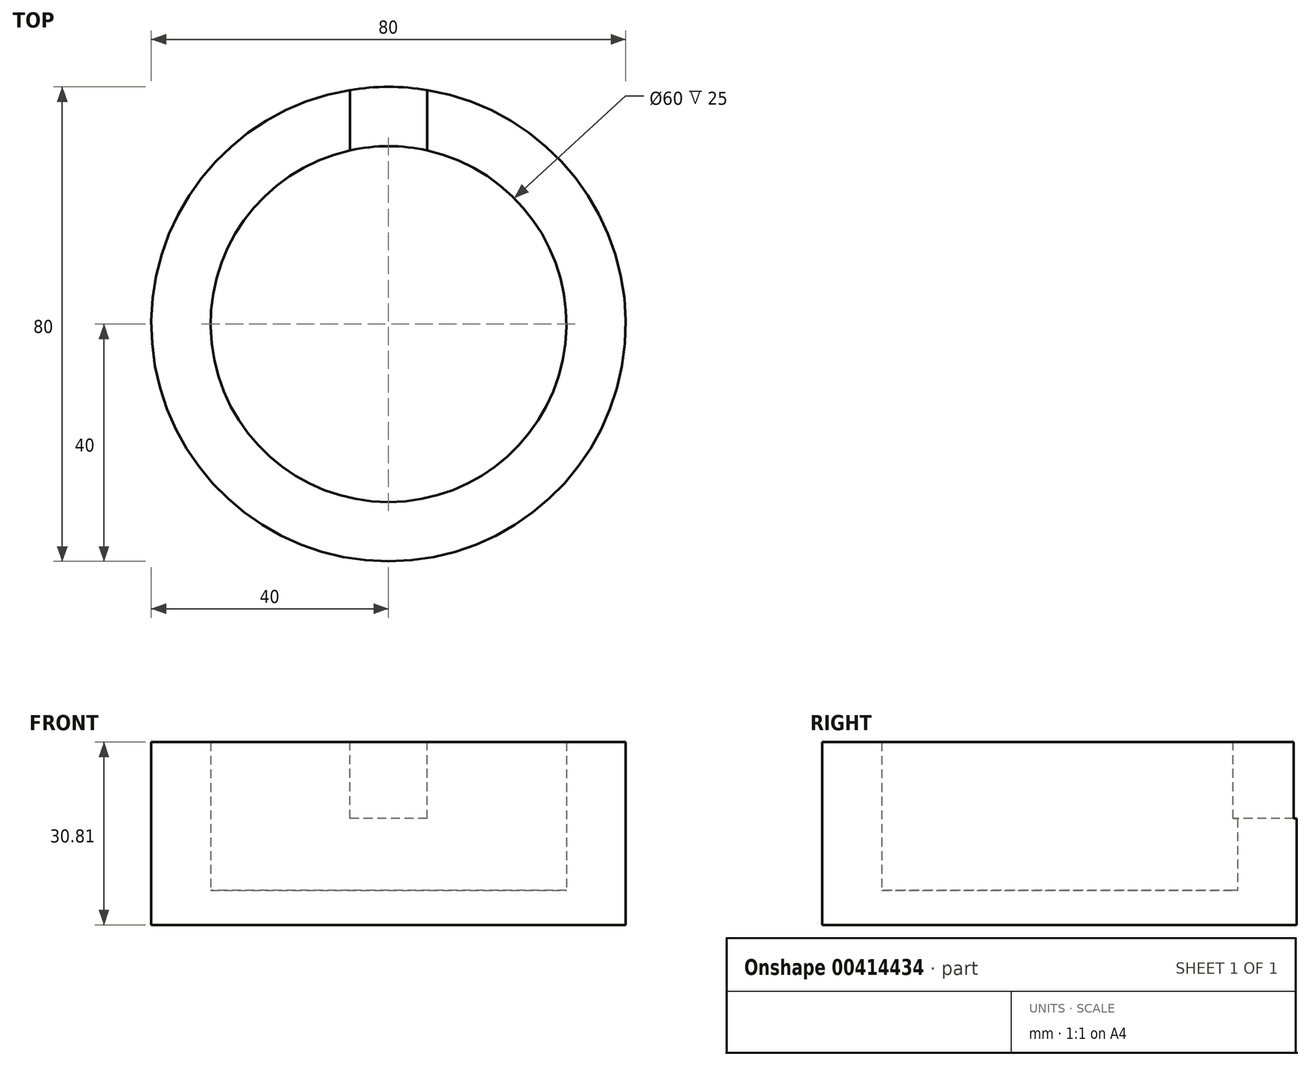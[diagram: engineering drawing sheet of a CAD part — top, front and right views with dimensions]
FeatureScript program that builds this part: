
annotation { "Feature Type Name" : "Feature", "Feature Type Description" : "" }
export const myFeature = defineFeature(function(context is Context, id is Id, definition is map)
    precondition{}
    {
        {
            var Q0;
            Q0=qCreatedBy(makeId("Top.planeOp"),FACE);
            var sketch = newSketch(context, id + "F0", { "sketchPlane" : qUnion([Q0])});
            skCircle(sketch, "E0", {"center": v(0, 0) * mm, "radius": 30 * mm});
            skCircle(sketch, "E1", {"center": v(0, 0) * mm, "radius": 40 * mm});
            skSolve(sketch);
        }
        {
            var Q0;
            Q0=makeQuery(id+"F0.imprint","IMPRINT",FACE,{"disambiguationData":[TD([[makeQuery(id+"F0.imprint","IMPRINT",EDGE,{"derivedFrom":sQuery(id+"F0.wireOp",EDGE,"E0")}),-1.0]])]});
            extrude(context, id + "F1", {"entities" : qUnion([Q0]), "depth" : 25 * mm});
        }
        {
            var Q0;
            Q0=makeQuery(id+"F1.opExtrude","CAP_FACE",FACE,{"disambiguationData":[OSD([sQuery(id+"F0.wireOp",EDGE,"E0"),sQuery(id+"F0.wireOp",EDGE,"E1")])],"isStart":false});
            var sketch = newSketch(context, id + "F2", { "sketchPlane" : qUnion([Q0])});
            skLineSegment(sketch, "E2", {"start": v(6.5, 39.47) * mm, "end": v(6.5, 29.29) * mm});
            skArc(sketch, "E3", {"start": v(6.5, 29.29) * mm, "mid": v(3.27, 29.82) * mm, "end": v(0, 30) * mm});
            skLineSegment(sketch, "E4", {"start": v(0, 30) * mm, "end": v(0, 40) * mm, "construction": true});
            skArc(sketch, "E5", {"start": v(6.5, 39.47) * mm, "mid": v(3.26, 39.87) * mm, "end": v(0, 40) * mm});
            skArc(sketch, "E6.MirrorCS", {"start": v(-6.5, 39.47) * mm, "mid": v(-3.26, 39.87) * mm, "end": v(0, 40) * mm});
            skLineSegment(sketch, "E7.MirrorCS", {"start": v(-6.5, 39.47) * mm, "end": v(-6.5, 29.29) * mm});
            skArc(sketch, "E8.MirrorCS", {"start": v(-6.5, 29.29) * mm, "mid": v(-3.27, 29.82) * mm, "end": v(0, 30) * mm});
            skSolve(sketch);
        }
        {
            var Q0;
            Q0 = qSketchRegion(id + "F2", true);
            extrude(context, id + "F3", {"entities" : qUnion([Q0]), "operationType" : NewBodyOperationType.REMOVE, "oppositeDirection" : true, "depth" : 12.9 * mm});
        }
        {
            var Q0;
            Q0=qCreatedBy(makeId("Right.planeOp"),FACE);
            var sketch = newSketch(context, id + "F4", { "sketchPlane" : qUnion([Q0])});
            skLineSegment(sketch, "E9", {"start": v(0, 0) * mm, "end": v(0, 57.63) * mm, "construction": true});
            skSolve(sketch);
        }
        {
            var Q0;
            Q0=makeQuery(id+"F1.opExtrude","CAP_FACE",FACE,{"disambiguationData":[OSD([sQuery(id+"F0.wireOp",EDGE,"E0"),sQuery(id+"F0.wireOp",EDGE,"E1")])],"isStart":true});
            var sketch = newSketch(context, id + "F5", { "sketchPlane" : qUnion([Q0])});
            skCircle(sketch, "E10", {"center": v(0, 0) * mm, "radius": 40 * mm});
            skSolve(sketch);
        }
        {
            var Q0;
            Q0 = qSketchRegion(id + "F5", true);
            var Q1;
            Q1=makeQuery(id+"F5.imprint","IMPRINT",FACE,{"disambiguationData":[TD([[makeQuery(id+"F5.imprint","IMPRINT",EDGE,{"derivedFrom":makeQuery(id+"F1.opExtrude","CAP_EDGE",EDGE,{"disambiguationData":[OSD([sQuery(id+"F0.wireOp",EDGE,"E0")])],"isStart":true})}),-1.0]])]});
            extrude(context, id + "F6", {"entities" : qUnion([Q0, Q1]), "operationType" : NewBodyOperationType.ADD, "depth" : 5.8 * mm});
        }
    });
